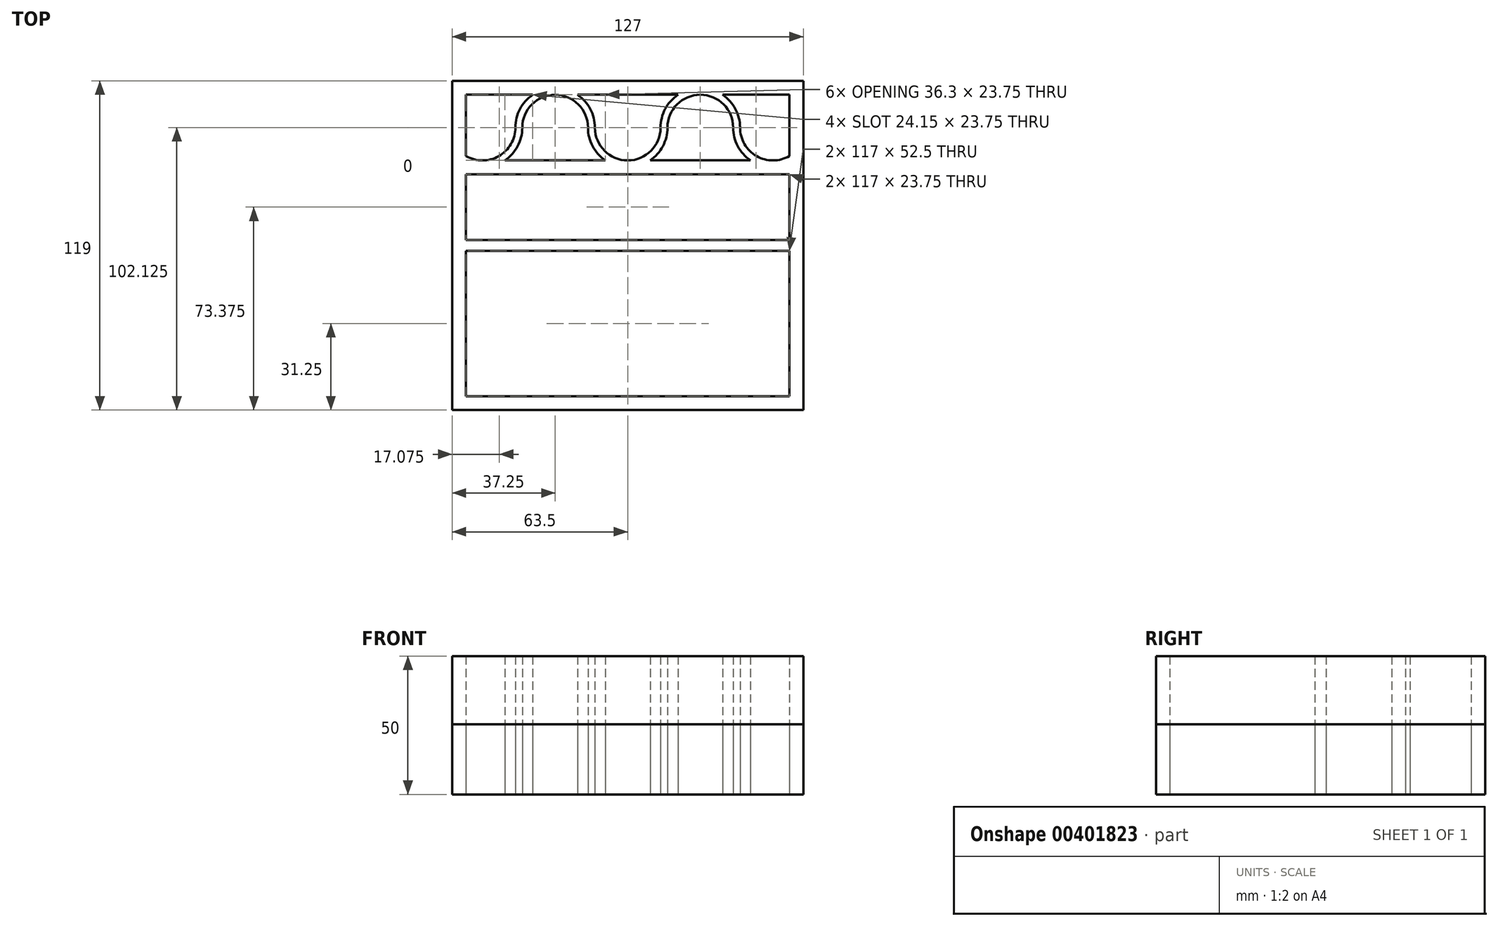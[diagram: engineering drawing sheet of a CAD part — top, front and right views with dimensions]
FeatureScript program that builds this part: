
annotation { "Feature Type Name" : "Feature", "Feature Type Description" : "" }
export const myFeature = defineFeature(function(context is Context, id is Id, definition is map)
    precondition{}
    {
        {
            var Q0;
            Q0=qCreatedBy(makeId("Top.planeOp"),FACE);
            var sketch = newSketch(context, id + "F0", { "sketchPlane" : qUnion([Q0])});
            skLineSegment(sketch, "E0.bottom", {"start": v(-63.5, 59.5) * mm, "end": v(63.5, 59.5) * mm});
            skLineSegment(sketch, "E0.top", {"start": v(-63.5, -59.5) * mm, "end": v(63.5, -59.5) * mm});
            skLineSegment(sketch, "E0.left", {"start": v(-63.5, 59.5) * mm, "end": v(-63.5, -59.5) * mm});
            skLineSegment(sketch, "E0.right", {"start": v(63.5, 59.5) * mm, "end": v(63.5, -59.5) * mm});
            skPoint(sketch, "E0.middle", {"position": v(0, 0) * mm});
            skLineSegment(sketch, "E1.top", {"start": v(-58.5, -54.5) * mm, "end": v(58.5, -54.5) * mm});
            skLineSegment(sketch, "E1.left", {"start": v(-58.5, 54.5) * mm, "end": v(-58.5, 32.38) * mm});
            skLineSegment(sketch, "E1.right", {"start": v(58.5, 54.5) * mm, "end": v(58.5, 32.38) * mm});
            skLineSegment(sketch, "E2.bottom", {"start": v(-58.5, 2) * mm, "end": v(58.5, 2) * mm});
            skLineSegment(sketch, "E2.top", {"start": v(-58.5, -2) * mm, "end": v(58.5, -2) * mm});
            skLineSegment(sketch, "E3.trimOffspring", {"start": v(58.5, -2) * mm, "end": v(58.5, -54.5) * mm});
            skLineSegment(sketch, "E4.trimOffspring", {"start": v(-58.5, -2) * mm, "end": v(-58.5, -54.5) * mm});
            skLineSegment(sketch, "E5", {"start": v(-58.5, -28.25) * mm, "end": v(58.5, -28.25) * mm});
            skLineSegment(sketch, "E6.top", {"start": v(-58.5, 25.75) * mm, "end": v(58.5, 25.75) * mm});
            skLineSegment(sketch, "E7.bottom", {"start": v(-58.5, -25.75) * mm, "end": v(58.5, -25.75) * mm});
            skLineSegment(sketch, "E7.top", {"start": v(-58.5, -30.75) * mm, "end": v(58.5, -30.75) * mm});
            skLineSegment(sketch, "E7.left", {"start": v(-58.5, -25.75) * mm, "end": v(-58.5, -30.75) * mm});
            skLineSegment(sketch, "E7.right", {"start": v(58.5, -25.75) * mm, "end": v(58.5, -30.75) * mm});
            skPoint(sketch, "E7.middle", {"position": v(0, -28.25) * mm});
            skLineSegment(sketch, "E8", {"start": v(0, 74.2) * mm, "end": v(0, -68.96) * mm, "construction": true});
            skLineSegment(sketch, "E9", {"start": v(-94.32, 0) * mm, "end": v(130.75, 0) * mm, "construction": true});
            skLineSegment(sketch, "E10", {"start": v(112.71, 42.62) * mm, "end": v(-89.48, 42.63) * mm, "construction": true});
            skLineSegment(sketch, "E11", {"start": v(106.14, 57) * mm, "end": v(-86.93, 57) * mm, "construction": true});
            skLineSegment(sketch, "E12", {"start": v(-63.5, 42.63) * mm, "end": v(-58.5, 42.63) * mm, "construction": true});
            skLineSegment(sketch, "E13", {"start": v(-44.4, 30.75) * mm, "end": v(-8.1, 30.75) * mm});
            skLineSegment(sketch, "E14", {"start": v(-58.5, 54.5) * mm, "end": v(-34.35, 54.5) * mm});
            skLineSegment(sketch, "E15", {"start": v(0, 30.75) * mm, "end": v(0, 25.75) * mm, "construction": true});
            skLineSegment(sketch, "E16", {"start": v(0, 28.25) * mm, "end": v(-92.13, 28.25) * mm, "construction": true});
            skLineSegment(sketch, "E17", {"start": v(0, 28.25) * mm, "end": v(127.37, 28.25) * mm, "construction": true});
            skArc(sketch, "E18", {"start": v(-14.38, 42.62) * mm, "mid": v(-12.71, 35.9) * mm, "end": v(-8.1, 30.75) * mm});
            skCircle(sketch, "E19", {"center": v(14.38, 42.62) * mm, "radius": 11.88 * mm, "construction": true});
            skArc(sketch, "E20", {"start": v(38.13, 42.62) * mm, "mid": v(26.25, 54.5) * mm, "end": v(14.38, 42.62) * mm});
            skCircle(sketch, "E21", {"center": v(40.63, 42.62) * mm, "radius": 11.88 * mm, "construction": true});
            skArc(sketch, "E22", {"start": v(38.13, 42.62) * mm, "mid": v(39.79, 35.9) * mm, "end": v(44.4, 30.75) * mm});
            skArc(sketch, "E23", {"start": v(40.63, 42.62) * mm, "mid": v(46.6, 32.32) * mm, "end": v(58.5, 32.38) * mm});
            skCircle(sketch, "E24", {"center": v(-14.38, 42.62) * mm, "radius": 11.88 * mm, "construction": true});
            skArc(sketch, "E25", {"start": v(-18.15, 30.75) * mm, "mid": v(-17.85, 30.96) * mm, "end": v(-17.55, 31.18) * mm});
            skArc(sketch, "E26", {"start": v(-14.38, 42.62) * mm, "mid": v(-26.25, 54.5) * mm, "end": v(-38.13, 42.62) * mm});
            skCircle(sketch, "E27", {"center": v(-40.63, 42.62) * mm, "radius": 11.88 * mm, "construction": true});
            skArc(sketch, "E28", {"start": v(-44.4, 30.75) * mm, "mid": v(-39.79, 35.9) * mm, "end": v(-38.13, 42.62) * mm});
            skArc(sketch, "E29", {"start": v(-58.5, 32.38) * mm, "mid": v(-46.6, 32.32) * mm, "end": v(-40.63, 42.63) * mm});
            skArc(sketch, "E30.trimOffspring", {"start": v(-43.8, 54.07) * mm, "mid": v(-44.1, 54.29) * mm, "end": v(-44.4, 54.5) * mm});
            skArc(sketch, "E31.trimOffspring", {"start": v(-11.88, 42.62) * mm, "mid": v(-13.54, 49.34) * mm, "end": v(-18.15, 54.5) * mm});
            skArc(sketch, "E32.trimOffspring", {"start": v(-34.35, 54.5) * mm, "mid": v(-38.96, 49.34) * mm, "end": v(-40.63, 42.62) * mm});
            skArc(sketch, "E33.trimOffspring", {"start": v(-11.88, 42.62) * mm, "mid": v(0, 30.75) * mm, "end": v(11.88, 42.62) * mm});
            skArc(sketch, "E34.trimOffspring", {"start": v(8.1, 30.75) * mm, "mid": v(12.71, 35.9) * mm, "end": v(14.38, 42.62) * mm});
            skArc(sketch, "E35.trimOffspring", {"start": v(18.15, 54.5) * mm, "mid": v(13.54, 49.34) * mm, "end": v(11.88, 42.62) * mm});
            skArc(sketch, "E36.trimOffspring", {"start": v(40.63, 42.62) * mm, "mid": v(38.96, 49.34) * mm, "end": v(34.35, 54.5) * mm});
            skLineSegment(sketch, "E37.trimOffspring", {"start": v(-58.5, 25.75) * mm, "end": v(-58.5, 2) * mm});
            skPoint(sketch, "E38.orphan", {"position": v(-58.5, 30.75) * mm});
            skLineSegment(sketch, "E39.trimOffspring", {"start": v(-18.15, 54.5) * mm, "end": v(18.15, 54.5) * mm});
            skLineSegment(sketch, "E40.trimOffspring", {"start": v(8.1, 30.75) * mm, "end": v(44.4, 30.75) * mm});
            skLineSegment(sketch, "E41.trimOffspring", {"start": v(34.35, 54.5) * mm, "end": v(58.5, 54.5) * mm});
            skLineSegment(sketch, "E42.trimOffspring", {"start": v(58.5, 25.75) * mm, "end": v(58.5, 2) * mm});
            skPoint(sketch, "E43.orphan", {"position": v(58.5, 30.75) * mm});
            skSolve(sketch);
        }
        {
            var Q0;
            Q0 = qSketchRegion(id + "F0", true);
            extrude(context, id + "F1", {"entities" : qUnion([Q0]), "depth" : 25.4 * mm});
        }
        {
            var Q0;
            Q0 = qSketchRegion(id + "F0", true);
            extrude(context, id + "F2", {"entities" : qUnion([Q0]), "depth" : 50 * mm});
        }
    });
